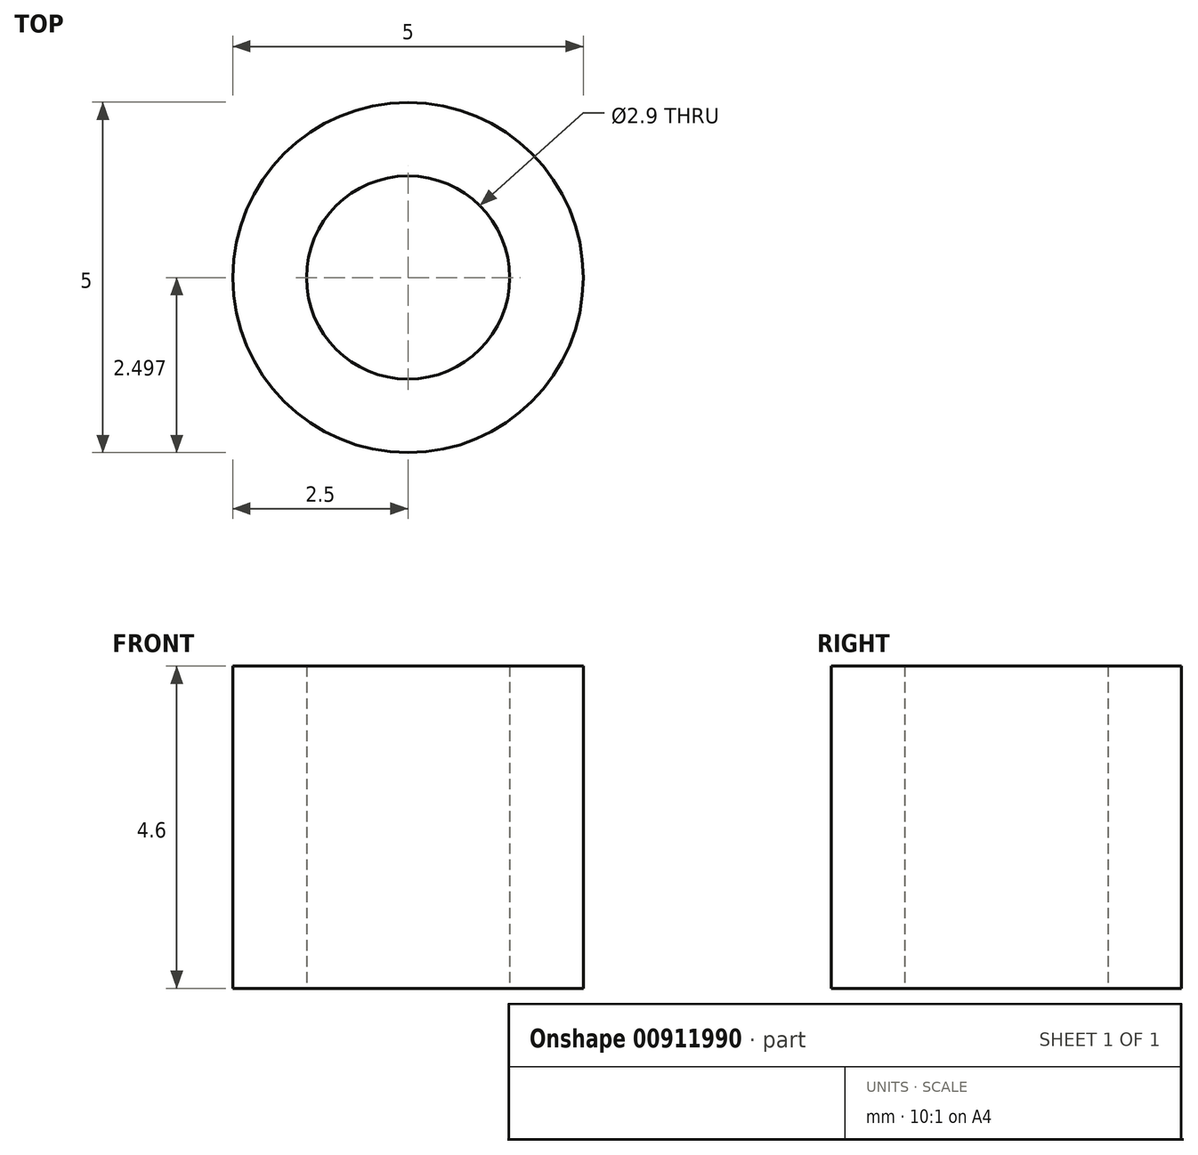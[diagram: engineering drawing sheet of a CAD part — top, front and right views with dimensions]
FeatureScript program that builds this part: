
annotation { "Feature Type Name" : "Feature", "Feature Type Description" : "" }
export const myFeature = defineFeature(function(context is Context, id is Id, definition is map)
    precondition{}
    {
        {
            var Q0;
            Q0=qCreatedBy(makeId("Top.planeOp"),FACE);
            var sketch = newSketch(context, id + "F0", { "sketchPlane" : qUnion([Q0])});
            skCircle(sketch, "E0", {"center": v(36.05, 42.8) * mm, "radius": 2.5 * mm});
            skPoint(sketch, "E0.first.point", {"position": v(36.35, 45.28) * mm});
            skPoint(sketch, "E0.second.point", {"position": v(37.42, 44.89) * mm});
            skPoint(sketch, "E0.third.point", {"position": v(34.8, 40.64) * mm});
            skSolve(sketch);
        }
        {
            var Q0;
            Q0=makeQuery(id+"F0.imprint","IMPRINT",FACE,{"disambiguationData":[TD([[makeQuery(id+"F0.imprint","IMPRINT",EDGE,{"derivedFrom":sQuery(id+"F0.wireOp",EDGE,"E0")}),1.0]])]});
            extrude(context, id + "F1", {"entities" : qUnion([Q0]), "depth" : 4.6 * mm, "offsetDistance" : 25.4 * mm});
        }
        {
            var Q0;
            Q0=sQuery(id+"F0.wireOp",VERTEX,"E0.center");
            var Q1;
            Q1=makeQuery(id+"F1.opExtrude","SWEPT_BODY",BODY,{"disambiguationData":[OSD([sQuery(id+"F0.wireOp",EDGE,"E0")])]});
            hole(context, id + "F2", {"style" : HoleStyle.SIMPLE, "endStyle" : HoleEndStyle.THROUGH, "oppositeDirection" : true, "holeDiameter" : 2.9 * mm, "majorDiameter" : 5 * mm, "isTappedThrough" : true, "tappedDepth" : 12 * mm, "tapClearance" : 3, "locations" : qUnion([Q0]), "scope" : qUnion([Q1])});
        }
    });
